# Revit family: NLRS_57_AIR_UN_rectangular-vandal-resistand-wall-grill-wtpp_LT_sacs
name_source: partatom
category: Air Terminals
units: mm (PartAtom-declared; Revit-internal decimal feet)

## family parameters
Always vertical = Yes
Cut with Voids When Loaded = No
Part Type = Normal
Room Calculation Point = No
Round Connector Dimension = Use Diameter
Shared = No
Work Plane-Based = No

## types (6) — shared parameters
Assembly Code = 57.00
Default Elevation = 2400 mm
Description = Vandal resistant supply grill WTPP
Manufacturer = Solid Air Climate Solutions
Model = WTPP
NLRS_C_content_datum_uitgifte = 17-09-2025
NLRS_C_content_provider = Solid Air Climate Solutions
NLRS_C_content_versie = 4.22.01
NLRS_C_description = Vandal resistant supply grill WTPP
SACS_Data_Hidden = WTPP
SACS_Type_Selector_1 = W_PP_Grill : RAL 9010-55
SACS_Type_Selector_2 = W_PP_Grill : RAL 9016-30
SACS_Type_Selector_3 = W_PP_Grill : RAL 9016-70
SACS_Type_Selector_4 = W_PP_Grill : Custom
URL = https://solid-air.nl

## per-type parameters (varying)
| type | Max Flow | Min Flow | SACS_Base_Index | SACS_Factor_LpF1 | SACS_Factor_LpF2 | SACS_Factor_PsF1 | SACS_Factor_PsF2 | SACS_Factor_WF1 | SACS_Factor_WF2 | SACS_Height2 | SACS_Width2 |
| 225x125 | 216.0 m³/h | 54.0 m³/h | 0 | -129.556448 | 30.475782 | 0.001803 | 2.001964 | 0.040159 | 0.98255 | 125 mm  [stored 0.410105 ft] | 225 mm  [stored 0.738189 ft] |
| 325x125 | 288.0 m³/h | 72.0 m³/h | 1 | -138.943994 | 29.998035 | 0.000732 | 2.001004 | 0.02067 | 1.036322 | 125 mm  [stored 0.410105 ft] | 325 mm  [stored 1.06627 ft] |
| 425x125 | 360.0 m³/h | 108.0 m³/h | 2 | -153.726083 | 31.215438 | 0.000371 | 2.0104 | 0.020586 | 0.987425 | 125 mm  [stored 0.410105 ft] | 425 mm  [stored 1.39436 ft] |
| 525x125 | 450.0 m³/h | 144.0 m³/h | 3 | -159.097525 | 31.11084 | 0.000238 | 2.005884 | 0.011489 | 1.047724 | 125 mm  [stored 0.410105 ft] | 525 mm  [stored 1.72244 ft] |
| 425x225 | 900.0 m³/h | 288.0 m³/h | 6 | -171.392574 | 30.469172 | 7.5e-05 | 1.995076 | 0.015689 | 0.987339 | 225 mm  [stored 0.738189 ft] | 425 mm  [stored 1.39436 ft] |
| 525x225 | 1080.0 m³/h | 360.0 m³/h | 7 | -177.605327 | 30.475782 | 3.6e-05 | 2.034971 | 0.018371 | 0.929329 | 225 mm  [stored 0.738189 ft] | 525 mm  [stored 1.72244 ft] |

note: [stored X ft] marks values corroborated as IEEE doubles in the binary element streams (Revit-internal decimal feet)

## geometry (parser evidence)
native form markers: Sweep x9
no freeform markers — native parametric forms only
